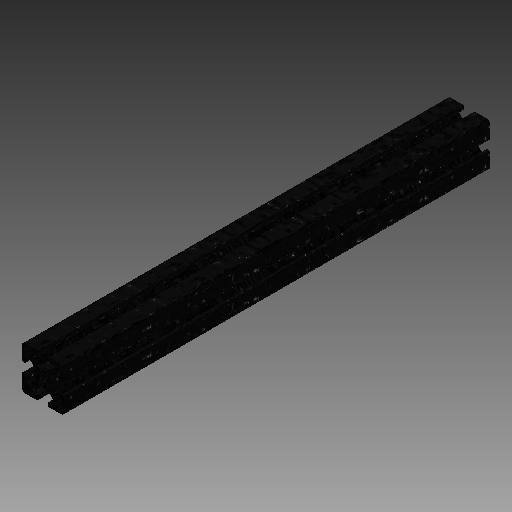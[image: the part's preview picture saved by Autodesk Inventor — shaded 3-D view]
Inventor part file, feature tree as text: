
AUTODESK INVENTOR PART (.ipt)
format: ipt  version: 2019 (Build 230136000, 136)  size: 266,752 bytes
history: native  units: in
note: dims shown in document units (in); Inventor stores cm internally (conversion verified against a paired STEP export)
features: plane x1, extrude x1, sketch x1
ambient origin geometry x8: Origin, YZ Plane, XZ Plane, XY Plane, X Axis, Y Axis, Z Axis, Center Point
bodies: Solid1 (feature_tree)
feature tree (3):
  plane  "Work Plane1"
  extrude  "Extrusion1"  [1 undecoded]
  sketch  "Sketch1"  dims[d0=14.75in d1=0.0in]
note: 1 required parameter value undecoded (feature->parameter linkage not recoverable at this tier; creation-order binding heuristic only, values carry confidence <= 0.55)
